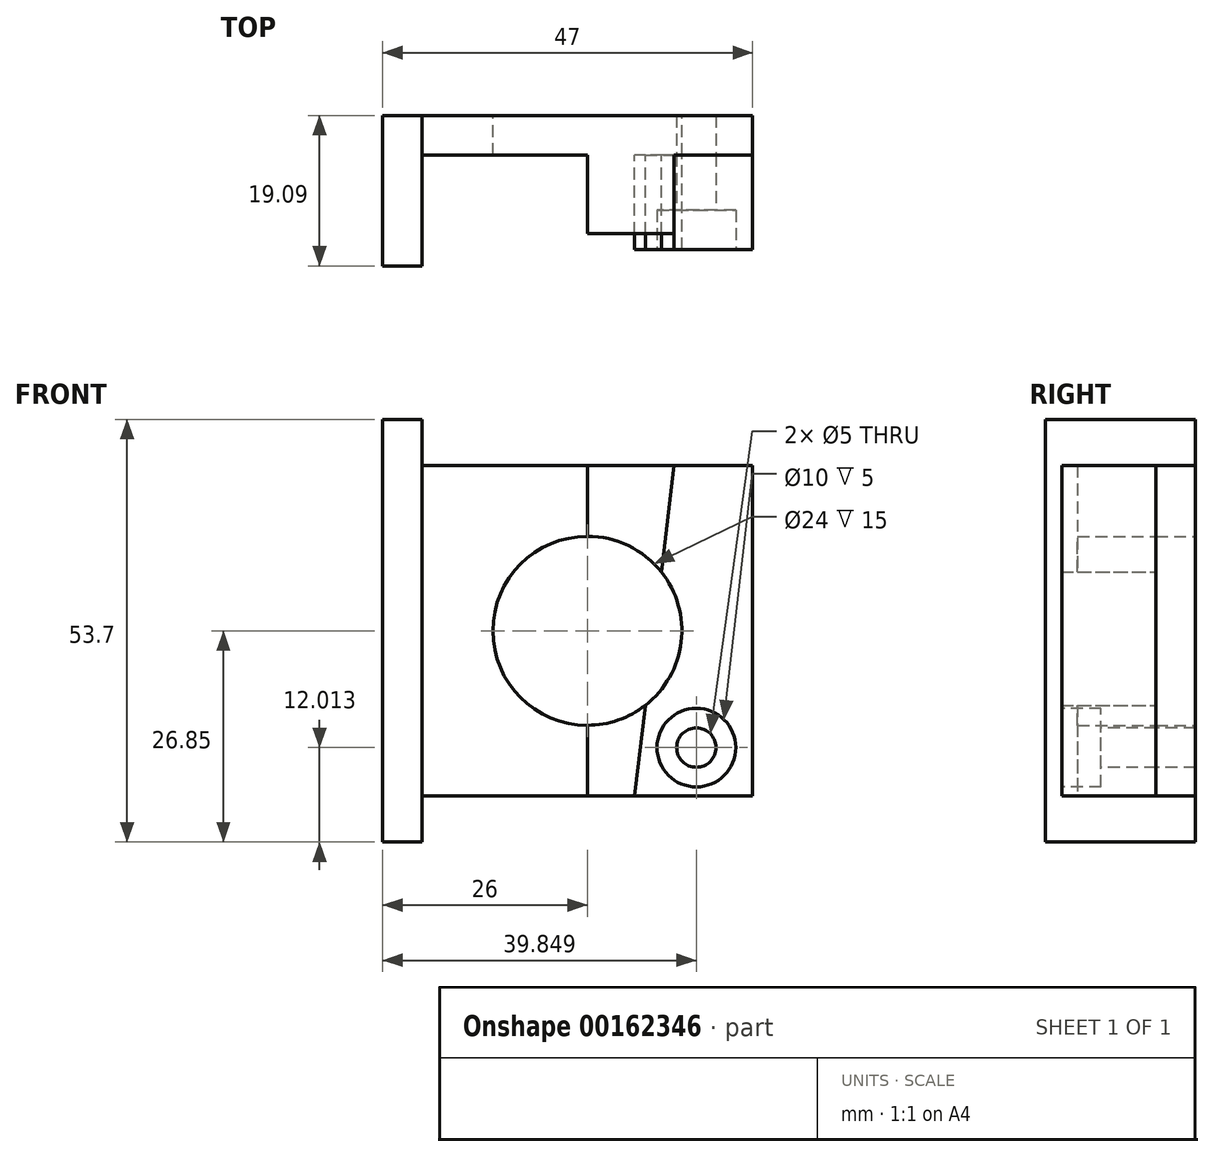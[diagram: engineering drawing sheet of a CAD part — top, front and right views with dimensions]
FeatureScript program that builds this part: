
annotation { "Feature Type Name" : "Feature", "Feature Type Description" : "" }
export const myFeature = defineFeature(function(context is Context, id is Id, definition is map)
    precondition{}
    {
        {
            var Q0;
            Q0=qCreatedBy(makeId("Front.planeOp"),FACE);
            var sketch = newSketch(context, id + "F0", { "sketchPlane" : qUnion([Q0])});
            skLineSegment(sketch, "E0.bottom", {"start": v(21, 21) * mm, "end": v(-21, 21) * mm});
            skLineSegment(sketch, "E0.top", {"start": v(21, -21) * mm, "end": v(-21, -21) * mm});
            skLineSegment(sketch, "E0.left", {"start": v(21, 21) * mm, "end": v(21, -21) * mm});
            skLineSegment(sketch, "E0.right", {"start": v(-21, 21) * mm, "end": v(-21, -21) * mm});
            skPoint(sketch, "E0.middle", {"position": v(0, 0) * mm});
            skCircle(sketch, "E1", {"center": v(0, 0) * mm, "radius": 12 * mm});
            skSolve(sketch);
        }
        {
            var Q0;
            Q0 = qSketchRegion(id + "F0", true);
            extrude(context, id + "F1", {"entities" : qUnion([Q0]), "depth" : 5 * mm});
        }
        {
            var Q0;
            Q0=makeQuery(id+"F1.opExtrude","SWEPT_FACE",FACE,{"disambiguationData":[OSD([sQuery(id+"F0.wireOp",EDGE,"E0.right")])]});
            var sketch = newSketch(context, id + "F2", { "sketchPlane" : qUnion([Q0])});
            skLineSegment(sketch, "E2.bottom", {"start": v(0, -26.85) * mm, "end": v(19.09, -26.85) * mm});
            skLineSegment(sketch, "E2.top", {"start": v(0, 26.85) * mm, "end": v(19.09, 26.85) * mm});
            skLineSegment(sketch, "E2.left", {"start": v(0, -26.85) * mm, "end": v(0, 26.85) * mm});
            skLineSegment(sketch, "E2.right", {"start": v(19.09, -26.85) * mm, "end": v(19.09, 26.85) * mm});
            skPoint(sketch, "E2.middle", {"position": v(9.54, 0) * mm});
            skPoint(sketch, "E2.middle.positionSnap0", {"position": v(5, 0) * mm});
            skPoint(sketch, "E2.centerSnap0", {"position": v(5, 0) * mm});
            skSolve(sketch);
        }
        {
            var Q0;
            Q0 = qSketchRegion(id + "F2", true);
            extrude(context, id + "F3", {"entities" : qUnion([Q0]), "operationType" : NewBodyOperationType.ADD, "depth" : 5 * mm});
        }
        {
            var Q0;
            Q0=makeQuery(id+"F1.opExtrude","CAP_FACE",FACE,{"disambiguationData":[OSD([sQuery(id+"F0.wireOp",EDGE,"E0.bottom"),sQuery(id+"F0.wireOp",EDGE,"E0.top"),sQuery(id+"F0.wireOp",EDGE,"E0.left"),sQuery(id+"F0.wireOp",EDGE,"E0.right"),sQuery(id+"F0.wireOp",EDGE,"E1")])],"isStart":false});
            var sketch = newSketch(context, id + "F4", { "sketchPlane" : qUnion([Q0])});
            skLineSegment(sketch, "E3", {"start": v(11, 21) * mm, "end": v(6, -21) * mm});
            skLineSegment(sketch, "E4", {"start": v(0, 21) * mm, "end": v(0, -21) * mm});
            skSolve(sketch);
        }
        {
            var Q0;
            Q0 = qSketchRegion(id + "F4", true);
            var Q1;
            {var subQ0=sQuery(id+"F4.wireOp",EDGE,"E3");var subQ1=makeQuery(id+"F1.opExtrude","CAP_EDGE",EDGE,{"disambiguationData":[OSD([sQuery(id+"F0.wireOp",EDGE,"E0.bottom")])],"isStart":false});var subQ2=makeQuery(id+"F4.imprint","INTERSECT",VERTEX,{"derivedFrom":[subQ1,subQ0]});Q1=makeQuery(id+"F4.imprint","IMPRINT",FACE,{"disambiguationData":[TD([[makeQuery(id+"F4.imprint","IMPRINT",EDGE,{"disambiguationData":[TD([[subQ2,-1.0]])],"derivedFrom":subQ0}),-1.0]])]});}
            var Q2;
            {var subQ0=sQuery(id+"F4.wireOp",EDGE,"E3");var subQ1=makeQuery(id+"F1.opExtrude","CAP_EDGE",EDGE,{"disambiguationData":[OSD([sQuery(id+"F0.wireOp",EDGE,"E0.top")])],"isStart":false});var subQ2=makeQuery(id+"F4.imprint","INTERSECT",VERTEX,{"derivedFrom":[subQ1,subQ0]});Q2=makeQuery(id+"F4.imprint","IMPRINT",FACE,{"disambiguationData":[TD([[makeQuery(id+"F4.imprint","IMPRINT",EDGE,{"disambiguationData":[TD([[subQ2,1.0]])],"derivedFrom":subQ0}),-1.0]])]});}
            extrude(context, id + "F5", {"entities" : qUnion([Q0, Q1, Q2]), "operationType" : NewBodyOperationType.ADD, "depth" : 10 * mm});
        }
        {
            var Q0;
            {var subQ0=sQuery(id+"F0.wireOp",EDGE,"E1");var subQ1=sQuery(id+"F0.wireOp",EDGE,"E0.left");var subQ3=sQuery(id+"F0.wireOp",EDGE,"E0.top");var subQ6=sQuery(id+"F0.wireOp",EDGE,"E0.bottom");Q0=makeQuery(id+"F5.boolean.opBoolean","SPLIT",FACE,{"disambiguationData":[TD([makeQuery(id+"F1.opExtrude","SWEPT_FACE",FACE,{"disambiguationData":[OSD([subQ1])]})])],"derivedFrom":makeQuery(id+"F1.opExtrude","CAP_FACE",FACE,{"disambiguationData":[OSD([subQ6,subQ3,subQ1,sQuery(id+"F0.wireOp",EDGE,"E0.right"),subQ0])],"isStart":false})});}
            extrude(context, id + "F6", {"entities" : qUnion([Q0]), "depth" : 12 * mm});
        }
        {
            var Q0;
            Q0=makeQuery(id+"F6.opExtrude","CAP_FACE",FACE,{"disambiguationData":[OSD([sQuery(id+"F0.wireOp",EDGE,"E0.bottom"),sQuery(id+"F0.wireOp",EDGE,"E0.top"),sQuery(id+"F0.wireOp",EDGE,"E0.left"),sQuery(id+"F0.wireOp",EDGE,"E0.right"),sQuery(id+"F0.wireOp",EDGE,"E1")])],"isStart":false});
            var sketch = newSketch(context, id + "F7", { "sketchPlane" : qUnion([Q0])});
            skPoint(sketch, "E5", {"position": v(13.85, -14.84) * mm});
            skSolve(sketch);
        }
        {
            var Q0;
            Q0=sQuery(id+"F7.wireOp",VERTEX,"E5");
            var Q1;
            Q1=makeQuery(id+"F1.opExtrude","SWEPT_BODY",BODY,{"disambiguationData":[OSD([sQuery(id+"F0.wireOp",EDGE,"E0.bottom"),sQuery(id+"F0.wireOp",EDGE,"E0.top"),sQuery(id+"F0.wireOp",EDGE,"E0.left"),sQuery(id+"F0.wireOp",EDGE,"E0.right"),sQuery(id+"F0.wireOp",EDGE,"E1")])]});
            var Q2;
            Q2=makeQuery(id+"F6.opExtrude","SWEPT_BODY",BODY,{"disambiguationData":[OSD([sQuery(id+"F0.wireOp",EDGE,"E0.bottom"),sQuery(id+"F0.wireOp",EDGE,"E0.top"),sQuery(id+"F0.wireOp",EDGE,"E0.left"),sQuery(id+"F0.wireOp",EDGE,"E0.right"),sQuery(id+"F0.wireOp",EDGE,"E1")])]});
            hole(context, id + "F8", {"style" : HoleStyle.C_BORE, "endStyle" : HoleEndStyle.THROUGH, "holeDiameter" : 5 * mm, "cBoreDiameter" : 10 * mm, "cBoreDepth" : 5 * mm, "locations" : qUnion([Q0]), "scope" : qUnion([Q1, Q2]), "isTappedThrough" : true});
        }
    });
